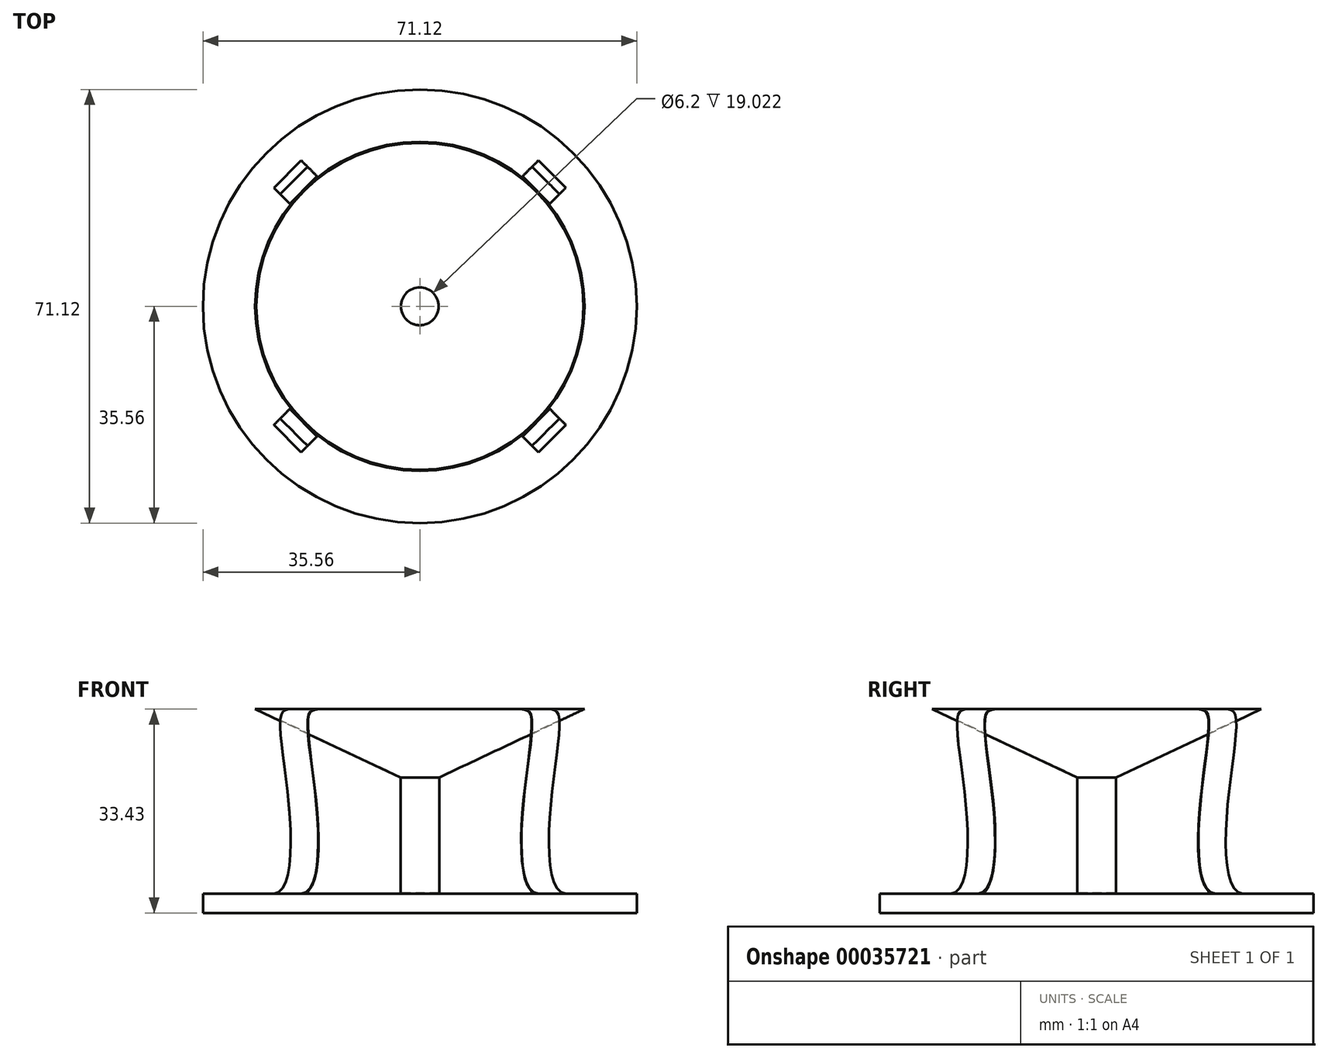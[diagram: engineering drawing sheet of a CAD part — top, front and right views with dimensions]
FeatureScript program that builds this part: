
annotation { "Feature Type Name" : "Feature", "Feature Type Description" : "" }
export const myFeature = defineFeature(function(context is Context, id is Id, definition is map)
    precondition{}
    {
        {
            var Q0;
            Q0=qCreatedBy(makeId("Top.planeOp"),FACE);
            var sketch = newSketch(context, id + "F0", { "sketchPlane" : qUnion([Q0])});
            skLineSegment(sketch, "E0.bottom", {"start": v(-38.1, 38.1) * mm, "end": v(38.1, 38.1) * mm});
            skLineSegment(sketch, "E0.top", {"start": v(-38.1, -38.1) * mm, "end": v(38.1, -38.1) * mm});
            skLineSegment(sketch, "E0.left", {"start": v(-38.1, 38.1) * mm, "end": v(-38.1, -38.1) * mm});
            skLineSegment(sketch, "E0.right", {"start": v(38.1, 38.1) * mm, "end": v(38.1, -38.1) * mm});
            skSolve(sketch);
        }
        {
            var Q0;
            Q0=makeQuery(id+"F0.imprint","IMPRINT",FACE,{"disambiguationData":[TD([[makeQuery(id+"F0.imprint","IMPRINT",EDGE,{"derivedFrom":sQuery(id+"F0.wireOp",EDGE,"E0.bottom")}),-1.0]])]});
            extrude(context, id + "F1", {"entities" : qUnion([Q0]), "depth" : 3.17 * mm});
        }
        {
            var Q0;
            Q0=makeQuery(id+"F1.opExtrude","CAP_FACE",FACE,{"disambiguationData":[OSD([sQuery(id+"F0.wireOp",EDGE,"E0.bottom"),sQuery(id+"F0.wireOp",EDGE,"E0.top"),sQuery(id+"F0.wireOp",EDGE,"E0.left"),sQuery(id+"F0.wireOp",EDGE,"E0.right")])],"isStart":false});
            var sketch = newSketch(context, id + "F2", { "sketchPlane" : qUnion([Q0])});
            skCircle(sketch, "E1", {"center": v(0, 0) * mm, "radius": 3.18 * mm});
            skSolve(sketch);
        }
        {
            var Q0;
            Q0=qSketchRegion(id+"F2",true);
            extrude(context, id + "F3", {"entities" : qUnion([Q0]), "depth" : 19.05 * mm});
        }
        {
            var Q0;
            Q0=qCreatedBy(makeId("Front.planeOp"),FACE);
            var sketch = newSketch(context, id + "F4", { "sketchPlane" : qUnion([Q0])});
            skLineSegment(sketch, "E2", {"start": v(0, 20.73) * mm, "end": v(26.99, 33.43) * mm});
            skLineSegment(sketch, "E3", {"start": v(26.99, 33.43) * mm, "end": v(0, 33.43) * mm});
            skLineSegment(sketch, "E4", {"start": v(0, 33.43) * mm, "end": v(0, 20.73) * mm});
            skLineSegment(sketch, "E5", {"start": v(3.18, 22.23) * mm, "end": v(3.18, 3.18) * mm});
            skSolve(sketch);
        }
        {
            var Q0;
            {var subQ1=sQuery(id+"F4.wireOp",EDGE,"E3");Q0=makeQuery(id+"F4.imprint","IMPRINT",FACE,{"disambiguationData":[TD([[makeQuery(id+"F4.imprint","IMPRINT",EDGE,{"derivedFrom":subQ1}),1.0]])]});}
            var Q1;
            Q1=sQuery(id+"F4.wireOp",EDGE,"E4");
            revolve(context, id + "F5", {"operationType" : NewBodyOperationType.ADD, "entities" : qUnion([Q0]), "axis" : qUnion([Q1]), "revolveType" : RevolveType.FULL});
        }
        {
            var Q0;
            Q0=makeQuery(id+"F5.opRevolve","SWEPT_FACE",FACE,{"disambiguationData":[OSD([sQuery(id+"F4.wireOp",EDGE,"E3")])]});
            shell(context, id + "F6", {"entities" : qUnion([Q0]), "thickness" : 0.08 * mm});
        }
        {
            var Q0;
            Q0=makeQuery(id+"F1.opExtrude","CAP_VERTEX",VERTEX,{"disambiguationData":[OSD([sQuery(id+"F0.wireOp",EDGE,"E0.top"),sQuery(id+"F0.wireOp",EDGE,"E0.right")])],"isStart":true});
            var Q1;
            Q1=makeQuery(id+"F1.opExtrude","CAP_VERTEX",VERTEX,{"disambiguationData":[OSD([sQuery(id+"F0.wireOp",EDGE,"E0.top"),sQuery(id+"F0.wireOp",EDGE,"E0.right")])],"isStart":false});
            var Q2;
            Q2=makeQuery(id+"F1.opExtrude","CAP_VERTEX",VERTEX,{"disambiguationData":[OSD([sQuery(id+"F0.wireOp",EDGE,"E0.bottom"),sQuery(id+"F0.wireOp",EDGE,"E0.left")])],"isStart":true});
            cPlane(context, id + "F7", {"entities" : qUnion([Q0, Q1, Q2]), "cplaneType" : CPlaneType.THREE_POINT, "offset" : 152.4 * mm, "width" : 152.4 * mm, "height" : 152.4 * mm});
        }
        {
            var Q0;
            Q0=qCreatedBy(id+"F7.planeOp",FACE);
            var sketch = newSketch(context, id + "F8", { "sketchPlane" : qUnion([Q0])});
            skLineSegment(sketch, "E6.0", {"start": v(-53.88, 3.18) * mm, "end": v(-53.88, 0) * mm});
            skLineSegment(sketch, "E7.0", {"start": v(0, 3.18) * mm, "end": v(-53.88, 3.18) * mm, "construction": true});
            skLineSegment(sketch, "E8.0", {"start": v(-26.99, 33.43) * mm, "end": v(26.99, 33.43) * mm, "construction": true});
            skFitSpline(sketch, "E9", {"points": [v(-26.99, 33.43) * mm, v(-28.8, 32.79) * mm, v(-26.99, 16.07) * mm, v(-30.68, 3.18) * mm], "startDerivative": vector(-9.05, -1.82) * mm, "endDerivative": vector(-28, 0) * mm});
            skSolve(sketch);
        }
        {
            var Q0;
            Q0=sQuery(id+"F8.wireOp",VERTEX,"E9.0.internal");
            var Q1;
            Q1=sQuery(id+"F8.wireOp",EDGE,"E7.0");
            cPlane(context, id + "F9", {"entities" : qUnion([Q0, Q1]), "cplaneType" : CPlaneType.CURVE_POINT, "offset" : 152.4 * mm, "width" : 152.4 * mm, "height" : 152.4 * mm});
        }
        {
            var Q0;
            Q0=qCreatedBy(id+"F9.planeOp",FACE);
            var sketch = newSketch(context, id + "F10", { "sketchPlane" : qUnion([Q0])});
            skPoint(sketch, "E10.0", {"position": v(0, 33.43) * mm});
            skLineSegment(sketch, "E11.bottom", {"start": v(-3.18, 33.43) * mm, "end": v(3.18, 33.43) * mm});
            skLineSegment(sketch, "E11.top", {"start": v(-3.17, 33.35) * mm, "end": v(3.18, 33.35) * mm});
            skLineSegment(sketch, "E11.left", {"start": v(-3.18, 33.43) * mm, "end": v(-3.18, 33.35) * mm});
            skLineSegment(sketch, "E11.right", {"start": v(3.18, 33.43) * mm, "end": v(3.18, 33.35) * mm});
            skSolve(sketch);
        }
        {
            var Q0;
            Q0=qSketchRegion(id+"F10",true);
            var Q1;
            Q1=sQuery(id+"F8.wireOp",EDGE,"E9");
            sweep(context, id + "F11", {"profiles" : qUnion([Q0]), "path" : qUnion([Q1])});
        }
        {
            var Q0;
            Q0=makeQuery(id+"F11.opSweep","SWEPT_BODY",BODY,{"disambiguationData":[OSD([sQuery(id+"F8.wireOp",EDGE,"E9"),sQuery(id+"F10.wireOp",EDGE,"E11.bottom"),sQuery(id+"F10.wireOp",EDGE,"E11.top"),sQuery(id+"F10.wireOp",EDGE,"E11.left"),sQuery(id+"F10.wireOp",EDGE,"E11.right")])]});
            var Q1;
            Q1=makeQuery(id+"F3.opExtrude","SWEPT_FACE",FACE,{"disambiguationData":[OSD([sQuery(id+"F2.wireOp",EDGE,"E1")])]});
            circularPattern(context, id + "F12", {"entities" : qUnion([Q0]), "axis" : qUnion([Q1]), "angle" : 90 * degree, "instanceCount" : round(4)});
        }
        {
            var Q0;
            Q0=makeQuery(id+"F1.opExtrude","CAP_FACE",FACE,{"disambiguationData":[OSD([sQuery(id+"F0.wireOp",EDGE,"E0.bottom"),sQuery(id+"F0.wireOp",EDGE,"E0.top"),sQuery(id+"F0.wireOp",EDGE,"E0.left"),sQuery(id+"F0.wireOp",EDGE,"E0.right")])],"isStart":true});
            var sketch = newSketch(context, id + "F13", { "sketchPlane" : qUnion([Q0])});
            skCircle(sketch, "E12", {"center": v(0, 0) * mm, "radius": 35.56 * mm});
            skLineSegment(sketch, "E13.0.0", {"start": v(-38.1, -38.1) * mm, "end": v(38.1, -38.1) * mm});
            skLineSegment(sketch, "E13.0.1", {"start": v(38.1, -38.1) * mm, "end": v(38.1, 38.1) * mm});
            skLineSegment(sketch, "E13.0.2", {"start": v(38.1, 38.1) * mm, "end": v(-38.1, 38.1) * mm});
            skLineSegment(sketch, "E13.0.3", {"start": v(-38.1, 38.1) * mm, "end": v(-38.1, -38.1) * mm});
            skSolve(sketch);
        }
        {
            var Q0;
            {var subQ0=sQuery(id+"F13.wireOp",EDGE,"E13.0.2");var subQ1=sQuery(id+"F13.wireOp",EDGE,"E12");var subQ2=makeQuery(id+"F13.imprint","INTERSECT",VERTEX,{"derivedFrom":[subQ1,subQ0]});Q0=makeQuery(id+"F13.imprint","IMPRINT",FACE,{"disambiguationData":[TD([[makeQuery(id+"F13.imprint","IMPRINT",EDGE,{"disambiguationData":[TD([[subQ2,-1.0]])],"derivedFrom":subQ1}),-1.0]])]});}
            var Q1;
            {var subQ0=sQuery(id+"F13.wireOp",EDGE,"E13.0.2");var subQ1=sQuery(id+"F13.wireOp",EDGE,"E12");var subQ2=makeQuery(id+"F13.imprint","INTERSECT",VERTEX,{"derivedFrom":[subQ1,subQ0]});Q1=makeQuery(id+"F13.imprint","IMPRINT",FACE,{"disambiguationData":[TD([[makeQuery(id+"F13.imprint","IMPRINT",EDGE,{"disambiguationData":[TD([[subQ2,1.0]])],"derivedFrom":subQ1}),-1.0]])]});}
            var Q2;
            {var subQ0=sQuery(id+"F13.wireOp",EDGE,"E13.0.1");var subQ1=sQuery(id+"F13.wireOp",EDGE,"E12");var subQ2=makeQuery(id+"F13.imprint","INTERSECT",VERTEX,{"derivedFrom":[subQ1,subQ0]});Q2=makeQuery(id+"F13.imprint","IMPRINT",FACE,{"disambiguationData":[TD([[makeQuery(id+"F13.imprint","IMPRINT",EDGE,{"disambiguationData":[TD([[subQ2,1.0]])],"derivedFrom":subQ1}),-1.0]])]});}
            var Q3;
            {var subQ0=sQuery(id+"F13.wireOp",EDGE,"E13.0.3");var subQ1=sQuery(id+"F13.wireOp",EDGE,"E12");var subQ2=makeQuery(id+"F13.imprint","INTERSECT",VERTEX,{"derivedFrom":[subQ1,subQ0]});Q3=makeQuery(id+"F13.imprint","IMPRINT",FACE,{"disambiguationData":[TD([[makeQuery(id+"F13.imprint","IMPRINT",EDGE,{"disambiguationData":[TD([[subQ2,-1.0]])],"derivedFrom":subQ1}),-1.0]])]});}
            extrude(context, id + "F14", {"entities" : qUnion([Q0, Q1, Q2, Q3]), "operationType" : NewBodyOperationType.REMOVE, "oppositeDirection" : true, "depth" : 25.4 * mm});
        }
    });
